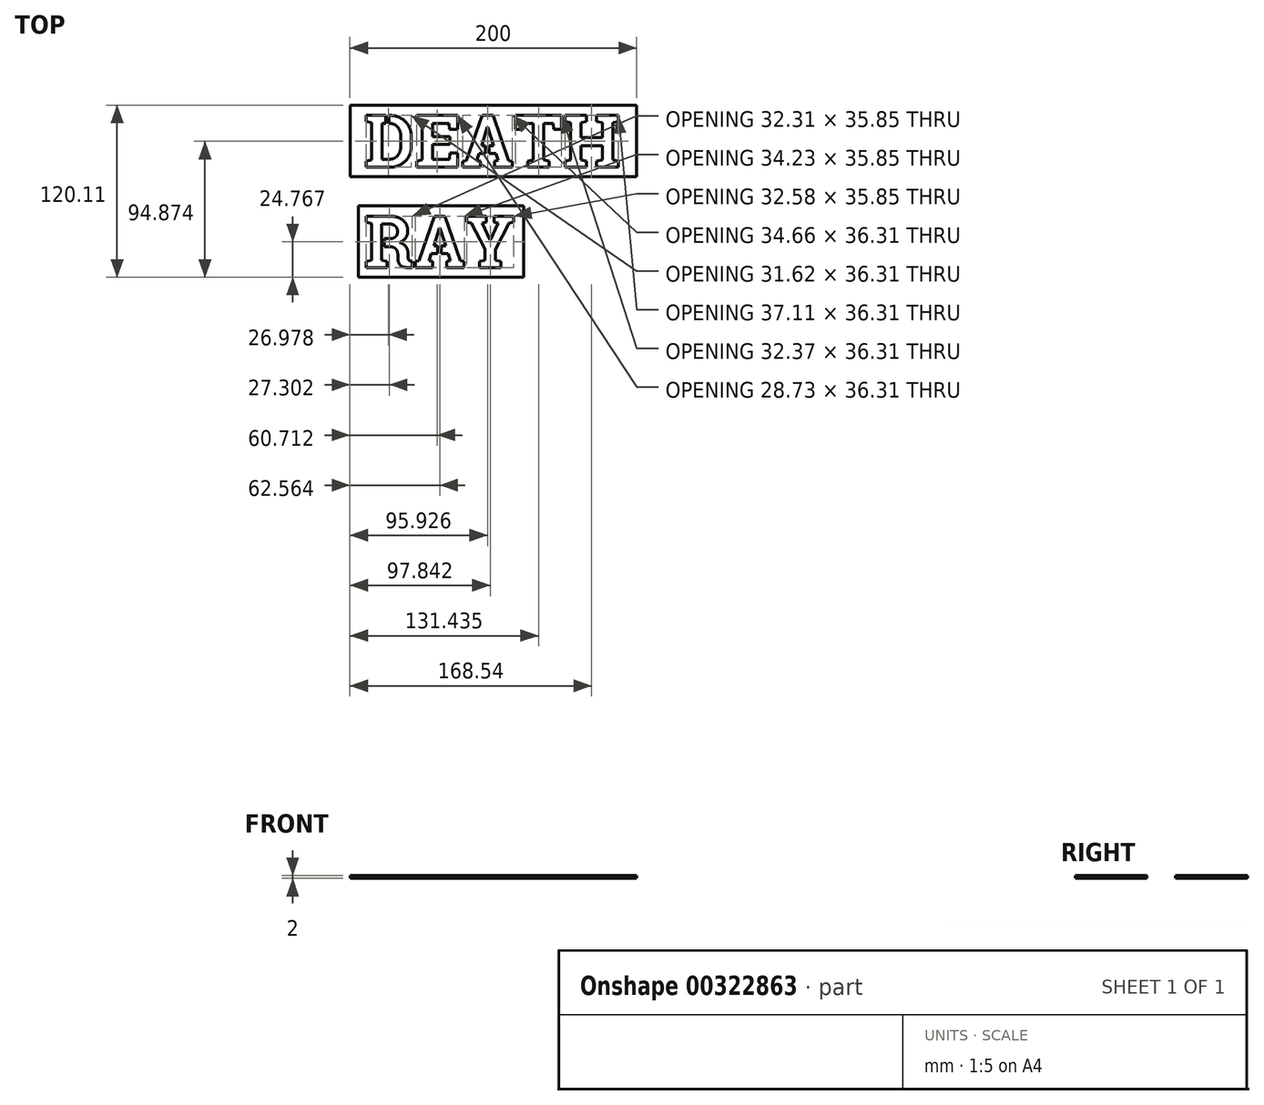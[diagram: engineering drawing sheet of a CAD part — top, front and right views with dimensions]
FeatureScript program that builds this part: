
annotation { "Feature Type Name" : "Feature", "Feature Type Description" : "" }
export const myFeature = defineFeature(function(context is Context, id is Id, definition is map)
    precondition{}
    {
        {
            var Q0;
            Q0=qCreatedBy(makeId("Top.planeOp"),FACE);
            var sketch = newSketch(context, id + "F0", { "sketchPlane" : qUnion([Q0])});
            skPoint(sketch, "E0.middle", {"position": v(0, 0) * mm});
            skText(sketch, "E1", { "text": "DEATH", "fontName": "RobotoSlab-Bold.ttf"});
            skLineSegment(sketch, "E2.bottom", {"start": v(190.23, 43.39) * mm, "end": v(-9.77, 43.39) * mm});
            skLineSegment(sketch, "E2.top", {"start": v(190.23, -6.61) * mm, "end": v(-9.77, -6.61) * mm});
            skLineSegment(sketch, "E2.left", {"start": v(190.23, 43.39) * mm, "end": v(190.23, -6.61) * mm});
            skLineSegment(sketch, "E2.right", {"start": v(-9.77, 43.39) * mm, "end": v(-9.77, -6.61) * mm});
            skPoint(sketch, "E2.middle", {"position": v(90.23, 18.39) * mm});
            skLineSegment(sketch, "E3.bottom", {"start": v(17.3, 30.47) * mm, "end": v(15.2, 30.47) * mm});
            skLineSegment(sketch, "E3.top", {"start": v(17.3, 43.08) * mm, "end": v(15.2, 43.08) * mm});
            skLineSegment(sketch, "E3.left", {"start": v(17.3, 30.47) * mm, "end": v(17.3, 43.08) * mm});
            skLineSegment(sketch, "E3.right", {"start": v(15.2, 30.47) * mm, "end": v(15.2, 43.08) * mm});
            skPoint(sketch, "E3.middle", {"position": v(16.25, 36.77) * mm});
            skLineSegment(sketch, "E4.bottom", {"start": v(87.3, 8.1) * mm, "end": v(84.6, 8.1) * mm});
            skLineSegment(sketch, "E4.top", {"start": v(87.3, 16.31) * mm, "end": v(84.6, 16.31) * mm});
            skLineSegment(sketch, "E4.left", {"start": v(87.3, 8.1) * mm, "end": v(87.3, 16.31) * mm});
            skLineSegment(sketch, "E4.right", {"start": v(84.6, 8.1) * mm, "end": v(84.6, 16.31) * mm});
            skPoint(sketch, "E4.middle", {"position": v(85.95, 12.2) * mm});
            const initialGuessF0  = {"E1": [0, 0, 1, 0, 0.03677]};
            skSetInitialGuess(sketch, initialGuessF0);
            skSolve(sketch);
        }
        {
            var Q0;
            {var subQ0=sQuery(id+"F0.wireOp",EDGE,"E1.sketch_text.stroke-59");Q0=makeQuery(id+"F0.imprint","IMPRINT",FACE,{"disambiguationData":[TD([[makeQuery(id+"F0.imprint","IMPRINT",EDGE,{"derivedFrom":subQ0}),1.0]])]});}
            var Q1;
            {var subQ5=sQuery(id+"F0.wireOp",EDGE,"E4.top");Q1=makeQuery(id+"F0.imprint","IMPRINT",FACE,{"disambiguationData":[TD([[makeQuery(id+"F0.imprint","IMPRINT",EDGE,{"derivedFrom":subQ5}),1.0]])]});}
            var Q2;
            {var subQ0=sQuery(id+"F0.wireOp",EDGE,"E4.left");var subQ1=sQuery(id+"F0.wireOp",EDGE,"E1.sketch_text.stroke-52");var subQ2=makeQuery(id+"F0.imprint","INTERSECT",VERTEX,{"derivedFrom":[subQ1,subQ0]});Q2=makeQuery(id+"F0.imprint","IMPRINT",FACE,{"disambiguationData":[TD([[makeQuery(id+"F0.imprint","IMPRINT",EDGE,{"disambiguationData":[TD([[subQ2,-1.0]])],"derivedFrom":subQ1}),-1.0]])]});}
            var Q3;
            {var subQ5=sQuery(id+"F0.wireOp",EDGE,"E4.bottom");Q3=makeQuery(id+"F0.imprint","IMPRINT",FACE,{"disambiguationData":[TD([[makeQuery(id+"F0.imprint","IMPRINT",EDGE,{"derivedFrom":subQ5}),-1.0]])]});}
            var Q4;
            {var subQ5=sQuery(id+"F0.wireOp",EDGE,"E3.bottom");Q4=makeQuery(id+"F0.imprint","IMPRINT",FACE,{"disambiguationData":[TD([[makeQuery(id+"F0.imprint","IMPRINT",EDGE,{"derivedFrom":subQ5}),-1.0]])]});}
            var Q5;
            {var subQ0=sQuery(id+"F0.wireOp",EDGE,"E3.right");var subQ1=sQuery(id+"F0.wireOp",EDGE,"E1.sketch_text.stroke-12");var subQ2=makeQuery(id+"F0.imprint","INTERSECT",VERTEX,{"derivedFrom":[subQ1,subQ0]});Q5=makeQuery(id+"F0.imprint","IMPRINT",FACE,{"disambiguationData":[TD([[makeQuery(id+"F0.imprint","IMPRINT",EDGE,{"disambiguationData":[TD([[subQ2,-1.0]])],"derivedFrom":subQ1}),-1.0]])]});}
            var Q6;
            {var subQ5=sQuery(id+"F0.wireOp",EDGE,"E3.top");Q6=makeQuery(id+"F0.imprint","IMPRINT",FACE,{"disambiguationData":[TD([[makeQuery(id+"F0.imprint","IMPRINT",EDGE,{"derivedFrom":subQ5}),1.0]])]});}
            var Q7;
            {var subQ5=sQuery(id+"F0.wireOp",EDGE,"E1.sketch_text.stroke-0");Q7=makeQuery(id+"F0.imprint","IMPRINT",FACE,{"disambiguationData":[TD([[makeQuery(id+"F0.imprint","IMPRINT",EDGE,{"derivedFrom":subQ5}),1.0]])]});}
            var Q8;
            {var subQ1=sQuery(id+"F0.wireOp",EDGE,"E1.sketch_text.stroke-13");Q8=makeQuery(id+"F0.imprint","IMPRINT",FACE,{"disambiguationData":[TD([[makeQuery(id+"F0.imprint","IMPRINT",EDGE,{"derivedFrom":subQ1}),1.0]])]});}
            extrude(context, id + "F1", {"entities" : qUnion([Q0, Q1, Q2, Q3, Q4, Q5, Q6, Q7, Q8]), "depth" : 2 * mm});
        }
        {
            var Q0;
            Q0=qCreatedBy(makeId("Top.planeOp"),FACE);
            var sketch = newSketch(context, id + "F2", { "sketchPlane" : qUnion([Q0])});
            skText(sketch, "E5", { "text": "RAY", "fontName": "RobotoSlab-Bold.ttf"});
            skLineSegment(sketch, "E6.bottom", {"start": v(111.23, -76.72) * mm, "end": v(-3.77, -76.72) * mm});
            skLineSegment(sketch, "E6.top", {"start": v(111.23, -26.72) * mm, "end": v(-3.77, -26.72) * mm});
            skLineSegment(sketch, "E6.left", {"start": v(111.23, -76.72) * mm, "end": v(111.23, -26.72) * mm});
            skLineSegment(sketch, "E6.right", {"start": v(-3.77, -76.72) * mm, "end": v(-3.77, -26.72) * mm});
            skPoint(sketch, "E6.middle", {"position": v(53.73, -51.72) * mm});
            skLineSegment(sketch, "E7.bottom", {"start": v(12.14, -57.77) * mm, "end": v(14.14, -57.77) * mm});
            skLineSegment(sketch, "E7.top", {"start": v(12.14, -46.41) * mm, "end": v(14.14, -46.41) * mm});
            skLineSegment(sketch, "E7.left", {"start": v(12.14, -57.77) * mm, "end": v(12.14, -46.41) * mm});
            skLineSegment(sketch, "E7.right", {"start": v(14.14, -57.77) * mm, "end": v(14.14, -46.41) * mm});
            skPoint(sketch, "E7.middle", {"position": v(13.14, -52.1) * mm});
            skLineSegment(sketch, "E8.bottom", {"start": v(53.83, -61.56) * mm, "end": v(51.33, -61.56) * mm});
            skLineSegment(sketch, "E8.top", {"start": v(53.83, -53.98) * mm, "end": v(51.33, -53.98) * mm});
            skLineSegment(sketch, "E8.left", {"start": v(53.83, -61.56) * mm, "end": v(53.83, -53.98) * mm});
            skLineSegment(sketch, "E8.right", {"start": v(51.33, -61.56) * mm, "end": v(51.33, -53.98) * mm});
            skPoint(sketch, "E8.middle", {"position": v(52.58, -57.77) * mm});
            const initialGuessF2  = {"E5": [0, -0.06988, 1, 0, 0.03631]};
            skSetInitialGuess(sketch, initialGuessF2);
            skSolve(sketch);
        }
        {
            var Q0;
            Q0 = qSketchRegion(id + "F2", true);
            var Q1;
            {var subQ5=sQuery(id+"F2.wireOp",EDGE,"E8.bottom");Q1=makeQuery(id+"F2.imprint","IMPRINT",FACE,{"disambiguationData":[TD([[makeQuery(id+"F2.imprint","IMPRINT",EDGE,{"derivedFrom":subQ5}),-1.0]])]});}
            var Q2;
            {var subQ0=sQuery(id+"F2.wireOp",EDGE,"E8.left");var subQ1=sQuery(id+"F2.wireOp",EDGE,"E5.sketch_text.stroke-46");var subQ2=makeQuery(id+"F2.imprint","INTERSECT",VERTEX,{"derivedFrom":[subQ1,subQ0]});Q2=makeQuery(id+"F2.imprint","IMPRINT",FACE,{"disambiguationData":[TD([[makeQuery(id+"F2.imprint","IMPRINT",EDGE,{"disambiguationData":[TD([[subQ2,-1.0]])],"derivedFrom":subQ1}),-1.0]])]});}
            var Q3;
            {var subQ5=sQuery(id+"F2.wireOp",EDGE,"E8.top");Q3=makeQuery(id+"F2.imprint","IMPRINT",FACE,{"disambiguationData":[TD([[makeQuery(id+"F2.imprint","IMPRINT",EDGE,{"derivedFrom":subQ5}),1.0]])]});}
            var Q4;
            {var subQ0=sQuery(id+"F2.wireOp",EDGE,"E5.sketch_text.stroke-53");Q4=makeQuery(id+"F2.imprint","IMPRINT",FACE,{"disambiguationData":[TD([[makeQuery(id+"F2.imprint","IMPRINT",EDGE,{"derivedFrom":subQ0}),1.0]])]});}
            var Q5;
            {var subQ0=sQuery(id+"F2.wireOp",EDGE,"E5.sketch_text.stroke-18");var subQ1=sQuery(id+"F2.wireOp",EDGE,"E5.sketch_text.stroke-17");var subQ2=makeQuery(id+"F2.imprint","INTERSECT",VERTEX,{"derivedFrom":[subQ1,subQ0]});Q5=makeQuery(id+"F2.imprint","IMPRINT",FACE,{"disambiguationData":[TD([[makeQuery(id+"F2.imprint","IMPRINT",EDGE,{"disambiguationData":[TD([[subQ2,1.0]])],"derivedFrom":subQ1}),1.0]])]});}
            var Q6;
            {var subQ0=sQuery(id+"F2.wireOp",EDGE,"E5.sketch_text.stroke-30");Q6=makeQuery(id+"F2.imprint","IMPRINT",FACE,{"disambiguationData":[TD([[makeQuery(id+"F2.imprint","IMPRINT",EDGE,{"derivedFrom":subQ0}),1.0]])]});}
            var Q7;
            {var subQ0=sQuery(id+"F2.wireOp",EDGE,"E5.sketch_text.stroke-35");var subQ1=sQuery(id+"F2.wireOp",EDGE,"E5.sketch_text.stroke-29");var subQ2=makeQuery(id+"F2.imprint","INTERSECT",VERTEX,{"derivedFrom":[subQ1,subQ0]});Q7=makeQuery(id+"F2.imprint","IMPRINT",FACE,{"disambiguationData":[TD([[makeQuery(id+"F2.imprint","IMPRINT",EDGE,{"disambiguationData":[TD([[subQ2,-1.0]])],"derivedFrom":subQ1}),1.0]])]});}
            var Q8;
            {var subQ7=sQuery(id+"F2.wireOp",EDGE,"E7.left");Q8=makeQuery(id+"F2.imprint","IMPRINT",FACE,{"disambiguationData":[TD([[makeQuery(id+"F2.imprint","IMPRINT",EDGE,{"derivedFrom":subQ7}),-1.0]])]});}
            extrude(context, id + "F3", {"entities" : qUnion([Q0, Q1, Q2, Q3, Q4, Q5, Q6, Q7, Q8]), "depth" : 2 * mm});
        }
        {
            var Q0;
            Q0=makeQuery(id+"F3.opExtrude","SWEPT_FACE",FACE,{"disambiguationData":[OSD([sQuery(id+"F2.wireOp",EDGE,"E7.left")])]});
            extrude(context, id + "F4", {"entities" : qUnion([Q0]), "operationType" : NewBodyOperationType.REMOVE, "oppositeDirection" : true, "depth" : .25 * mm});
        }
    });
